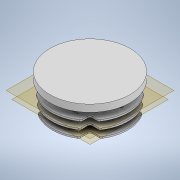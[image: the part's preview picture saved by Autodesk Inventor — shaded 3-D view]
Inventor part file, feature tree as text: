
AUTODESK INVENTOR PART (.ipt)
format: ipt  version: 2020 (Build 240168000, 168)  size: 353,280 bytes
history: native  units: mm
features: extrude x5, sketch x5, other x2, fillet x2
ambient origin geometry x8: Origin, YZ Plane, XZ Plane, XY Plane, X Axis, Y Axis, Z Axis, Center Point
bodies: Solide1 (feature_tree)
feature tree (14):
  extrude  "Extrusion1"  Depth=15.2mm
  extrude  "Extrusion2"  Depth=27.1mm
  extrude  "Extrusion4"  Depth=1.3mm
  other  "Plan de construction2"
  extrude  "Extrusion5"  Depth=31.0mm
  other  "Plan de construction3"
  extrude  "Extrusion6"  Depth=15.35mm TaperAngle=0.0deg
  fillet  "Congé1"  Radius=1.3mm
  fillet  "Congé2"  Radius=5.6mm
  sketch  "Esquisse1"
  sketch  "Esquisse2"
  sketch  "Esquisse5"
  sketch  "Esquisse6"
  sketch  "Esquisse7"
